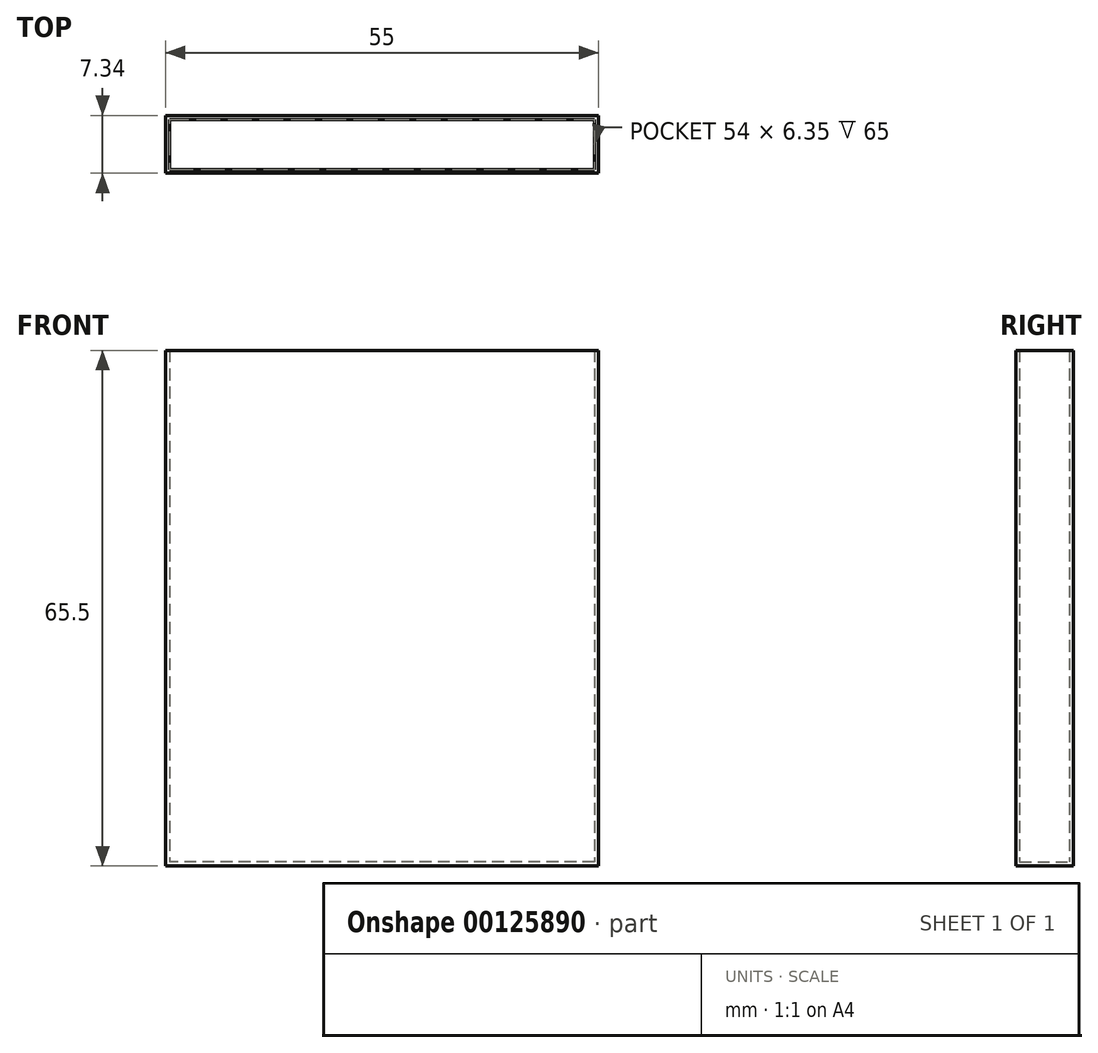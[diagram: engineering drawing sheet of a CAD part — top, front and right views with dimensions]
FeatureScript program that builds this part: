
annotation { "Feature Type Name" : "Feature", "Feature Type Description" : "" }
export const myFeature = defineFeature(function(context is Context, id is Id, definition is map)
    precondition{}
    {
        {
            var Q0;
            Q0=qCreatedBy(makeId("Top.planeOp"),FACE);
            var sketch = newSketch(context, id + "F0", { "sketchPlane" : qUnion([Q0])});
            skLineSegment(sketch, "E0.bottom", {"start": v(27, -3.17) * mm, "end": v(-27, -3.18) * mm});
            skLineSegment(sketch, "E0.top", {"start": v(27, 3.18) * mm, "end": v(-27, 3.17) * mm});
            skLineSegment(sketch, "E0.left", {"start": v(27, -3.17) * mm, "end": v(27, 3.18) * mm});
            skLineSegment(sketch, "E0.right", {"start": v(-27, -3.18) * mm, "end": v(-27, 3.17) * mm});
            skPoint(sketch, "E0.middle", {"position": v(0, 0) * mm});
            skSolve(sketch);
        }
        {
            var Q0;
            Q0=makeQuery(id+"F0.imprint","IMPRINT",FACE,{"disambiguationData":[TD([[makeQuery(id+"F0.imprint","IMPRINT",EDGE,{"derivedFrom":sQuery(id+"F0.wireOp",EDGE,"E0.bottom")}),-1.0]])]});
            extrude(context, id + "F1", {"entities" : qUnion([Q0]), "depth" : 65 * mm, "offsetDistance" : 25 * mm});
        }
        {
            var Q0;
            Q0=makeQuery(id+"F1.opExtrude","CAP_FACE",FACE,{"disambiguationData":[OSD([sQuery(id+"F0.wireOp",EDGE,"E0.bottom"),sQuery(id+"F0.wireOp",EDGE,"E0.top"),sQuery(id+"F0.wireOp",EDGE,"E0.left"),sQuery(id+"F0.wireOp",EDGE,"E0.right")])],"isStart":false});
            shell(context, id + "F2", {"entities" : qUnion([Q0]), "thickness" : .5 * mm, "oppositeDirection" : true});
        }
    });
